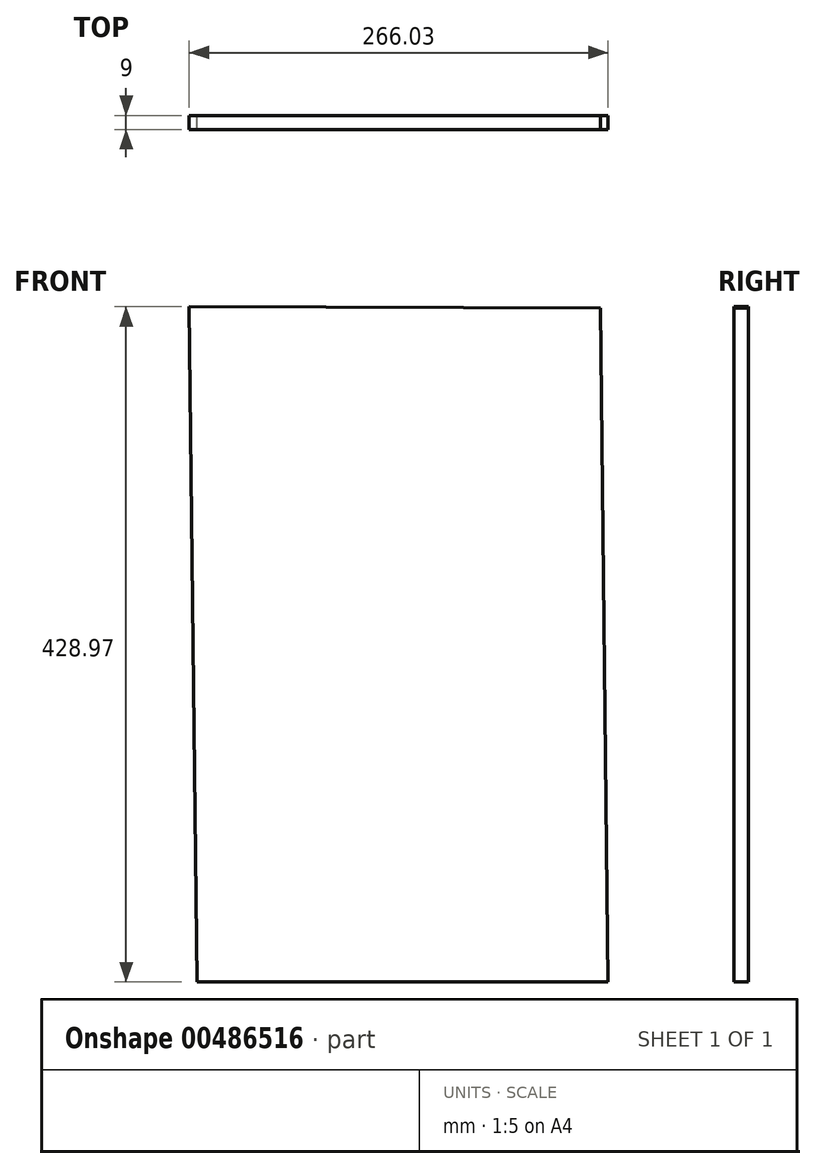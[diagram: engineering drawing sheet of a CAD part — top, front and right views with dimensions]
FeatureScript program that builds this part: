
annotation { "Feature Type Name" : "Feature", "Feature Type Description" : "" }
export const myFeature = defineFeature(function(context is Context, id is Id, definition is map)
    precondition{}
    {
        {
            var Q0;
            Q0=qCreatedBy(makeId("Front.planeOp"),FACE);
            var sketch = newSketch(context, id + "F0", { "sketchPlane" : qUnion([Q0])});
            skArc(sketch, "E0", {"start": v(765.46, 1224) * mm, "mid": v(1495.6, 924.81) * mm, "end": v(1798, 196) * mm});
            skLineSegment(sketch, "E1", {"start": v(1798, 196) * mm, "end": v(1798, 0) * mm});
            skLineSegment(sketch, "E2", {"start": v(1798, 0) * mm, "end": v(0, 0) * mm});
            skLineSegment(sketch, "E3", {"start": v(0, 0) * mm, "end": v(-5.8, 613.15) * mm});
            skCircle(sketch, "E4", {"center": v(194.06, 100) * mm, "radius": 30 * mm});
            skLineSegment(sketch, "E5", {"start": v(910, 0) * mm, "end": v(905, 428) * mm});
            skLineSegment(sketch, "E6", {"start": v(643.97, 428.97) * mm, "end": v(905, 428) * mm});
            skLineSegment(sketch, "E7", {"start": v(-424.54, 1215) * mm, "end": v(-422.04, 954.01) * mm});
            skLineSegment(sketch, "E8", {"start": v(-422.04, 954.01) * mm, "end": v(-5.8, 613.15) * mm});
            skLineSegment(sketch, "E9", {"start": v(-424.54, 1215) * mm, "end": v(765.46, 1224) * mm});
            skLineSegment(sketch, "E10", {"start": v(765.46, 1224) * mm, "end": v(772.98, 428.5) * mm});
            skLineSegment(sketch, "E11", {"start": v(643.97, 428.97) * mm, "end": v(649, 0) * mm});
            skSolve(sketch);
        }
        {
            var Q0;
            {var subQ1=sQuery(id+"F0.wireOp",EDGE,"E5");Q0=makeQuery(id+"F0.imprint","IMPRINT",FACE,{"disambiguationData":[TD([[makeQuery(id+"F0.imprint","IMPRINT",EDGE,{"derivedFrom":subQ1}),1.0]])]});}
            extrude(context, id + "F1", {"entities" : qUnion([Q0]), "depth" : 9 * mm, "offsetDistance" : 25 * mm});
        }
    });
